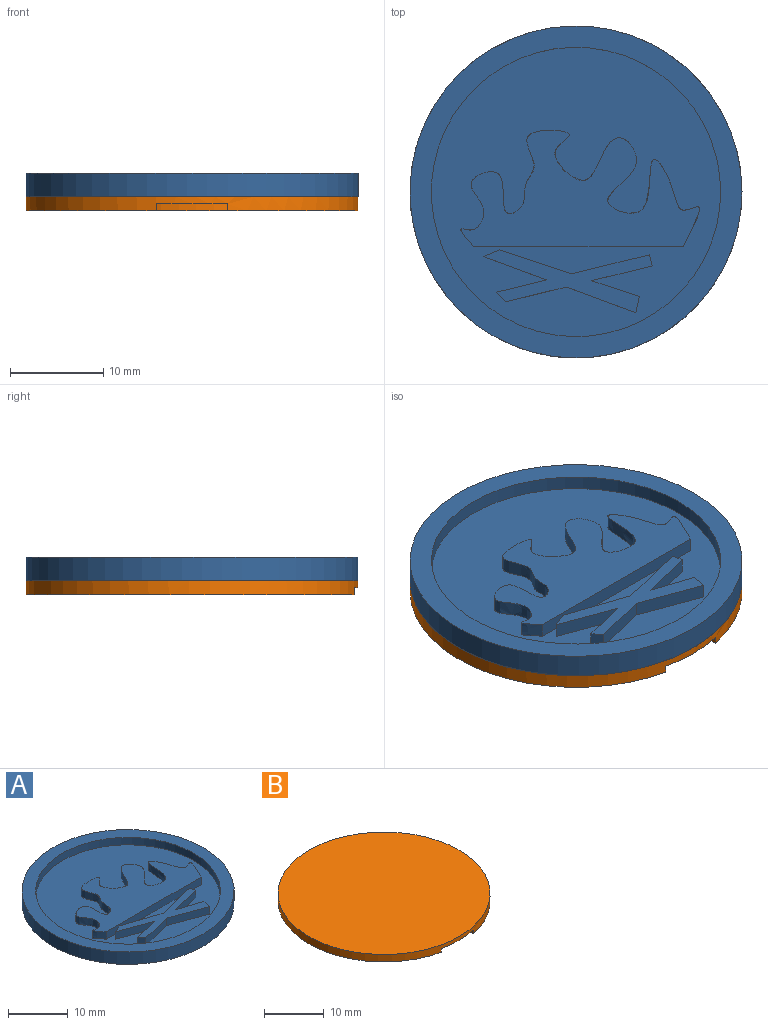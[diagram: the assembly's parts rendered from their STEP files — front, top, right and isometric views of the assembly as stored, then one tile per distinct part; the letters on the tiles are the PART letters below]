
ASSEMBLY  parts=2 mates=1
PART A: 21 faces, bbox 35.6x35.6x2.5 mm
  f0: plane 30.99x30.99mm, normal (0,0,1), area 534.1mm2, adj f4,f5,f6,f8,f9,f10,f11,f12
  f1: cylinder r=17.78mm len=35.56mm, axis (0,0,-1), area 283.8mm2, adj f2,f3
  f2: plane 35.56x35.56mm, normal (0,0,1), area 239mm2, adj f1,f4
  f3: plane 35.56x35.56mm, normal (0,0,-1), area 993.1mm2, adj f1
  f4: cylinder r=15.49mm len=30.99mm, axis (0,0,1), area 148.4mm2, adj f0,f2
  f5: extruded ~25.4x12.45mm, area 109.6mm2, adj f0,f6,f7
  f6: plane 22.45x1.52mm, normal (0,-1,0), area 34.2mm2, adj f0,f5,f7
  f7: plane 26.1x12.73mm, normal (0,0,1), area 178.2mm2, adj f5,f6
  f8: plane 7.73x2.57mm, normal (0.32,0.95,0), area 12.4mm2, adj f0,f9,f19,f20
  f9: plane 1.72x1.52mm, normal (-0.38,0.92,0), area 2.8mm2, adj f0,f8,f10,f20
  f10: plane 6.81x2.5mm, normal (-0.35,-0.94,0), area 11.1mm2, adj f0,f9,f11,f20
  f11: plane 5.37x1.52mm, normal (-0.24,0.97,0), area 8.4mm2, adj f0,f10,f12,f20
  f12: plane 1.52x1.04mm, normal (-0.76,-0.66,0), area 2.1mm2, adj f0,f11,f13,f20
  f13: plane 6.53x1.6mm, normal (0.24,-0.97,0), area 10.2mm2, adj f0,f12,f14,f20
  f14: plane 7.48x2.75mm, normal (-0.35,-0.94,0), area 12.1mm2, adj f0,f13,f15,f20
  f15: plane 1.74x1.52mm, normal (0.98,-0.21,0), area 2.7mm2, adj f0,f14,f16,f20
  f16: plane 5.08x1.69mm, normal (0.32,0.95,0), area 8.2mm2, adj f0,f15,f17,f20
  f17: plane 6.44x1.58mm, normal (0.24,-0.97,0), area 10.1mm2, adj f0,f16,f18,f20
  f18: plane 1.52x1.19mm, normal (0.97,0.24,0), area 1.9mm2, adj f0,f17,f19,f20
  f19: plane 8.34x2.05mm, normal (-0.24,0.97,0), area 13.1mm2, adj f0,f8,f18,f20
  f20: plane 18.08x6.73mm, normal (0,0,1), area 41.9mm2, adj f8,f9,f10,f11,f12,f13,f14,f15
PART B: 170 faces, bbox 35.6x35.6x1.5 mm
  f0: plane 30.99x30.99mm, normal (0,0,-1), area 549.6mm2, adj f4,f5,f6,f7,f8,f9,f10,f11
  f1: plane 35.56x35.15mm, normal (0,0,-1), area 175mm2, adj f2,f165,f167,f169
  f2: cylinder r=17.78mm len=35.56mm, axis (0,0,-1), area 164.4mm2, adj f1,f3,f165,f167,f168
  f3: plane 35.56x35.56mm, normal (0,0,1), area 993.1mm2, adj f2
  f4: plane 1.49x0.76mm, normal (0,-1,0), area 1.1mm2, adj f0,f5,f15,f16
  f5: plane 7.05x0.76mm, normal (-1,0,0), area 5.4mm2, adj f0,f4,f6,f16
  f6: plane 1.49x0.76mm, normal (0,1,0), area 1.1mm2, adj f0,f5,f7,f16
  f7: plane 2.76x0.76mm, normal (1,0,0), area 2.1mm2, adj f0,f6,f8,f16
  f8: plane 2.79x0.76mm, normal (0,1,0), area 2.1mm2, adj f0,f7,f9,f16
  f9: plane 2.76x0.76mm, normal (-1,0,0), area 2.1mm2, adj f0,f8,f10,f16
  f10: plane 1.5x0.76mm, normal (0,1,0), area 1.1mm2, adj f0,f9,f11,f16
  f11: plane 7.05x0.76mm, normal (1,0,0), area 5.4mm2, adj f0,f10,f12,f16
  f12: plane 1.5x0.76mm, normal (0,-1,0), area 1.1mm2, adj f0,f11,f13,f16
  f13: plane 3.04x0.76mm, normal (-1,0,0), area 2.3mm2, adj f0,f12,f14,f16
  f14: plane 2.79x0.76mm, normal (0,-1,0), area 2.1mm2, adj f0,f13,f15,f16
  f15: plane 3.04x0.76mm, normal (1,0,0), area 2.3mm2, adj f0,f4,f14,f16
  f16: plane 7.05x5.78mm, normal (0,0,-1), area 24.5mm2, adj f4,f5,f6,f7,f8,f9,f10,f11
  f17: plane 7.05x0.76mm, normal (-1,0,0), area 5.4mm2, adj f0,f18,f41,f42
  f18: plane 2.19x0.76mm, normal (0,1,0), area 1.7mm2, adj f0,f17,f19,f42
  f19: extruded ~2.18x0.76mm, area 1.7mm2, adj f0,f18,f20,f42
  f20: extruded ~1.36x0.76mm, area 1.2mm2, adj f0,f19,f21,f42
  f21: extruded ~1.04x0.76mm, area 0.8mm2, adj f0,f20,f22,f42
  f22: extruded ~0.79x0.76mm, area 0.7mm2, adj f0,f21,f23,f42
  f23: plane 0.76x0.05mm, normal (1,0,0), area 0mm2, adj f0,f22,f24,f42
  f24: extruded ~0.97x0.76mm, area 0.9mm2, adj f0,f23,f25,f42
  f25: extruded ~1.09x0.76mm, area 0.9mm2, adj f0,f24,f26,f42
  f26: extruded ~1.51x0.76mm, area 1.3mm2, adj f0,f25,f27,f42
  f27: extruded ~1.89x0.76mm, area 1.5mm2, adj f0,f26,f41,f42
  f28: plane 0.93x0.76mm, normal (0,-1,0), area 0.7mm2, adj f29,f39,f42,f44
  f29: plane 1.84x0.76mm, normal (1,0,0), area 1.4mm2, adj f28,f30,f42,f44
  f30: plane 0.97x0.76mm, normal (0,1,0), area 0.7mm2, adj f29,f31,f42,f44
  f31: extruded ~0.91x0.76mm, area 0.7mm2, adj f30,f32,f42,f44
  f32: extruded ~0.76x0.72mm, area 0.6mm2, adj f31,f39,f42,f44
  f33: plane 1.57x0.76mm, normal (1,0,0), area 1.2mm2, adj f34,f40,f42,f43
  f34: plane 0.87x0.76mm, normal (0,1,0), area 0.7mm2, adj f33,f35,f42,f43
  f35: extruded ~0.88x0.76mm, area 0.7mm2, adj f34,f36,f42,f43
  f36: extruded ~0.76x0.62mm, area 0.5mm2, adj f35,f37,f42,f43
  f37: extruded ~0.76x0.58mm, area 0.5mm2, adj f36,f38,f42,f43
  f38: extruded ~0.94x0.76mm, area 0.7mm2, adj f37,f40,f42,f43
  f39: extruded ~1.25x0.88mm, area 1.3mm2, adj f28,f32,f42,f44
  f40: plane 0.79x0.76mm, normal (0,-1,0), area 0.6mm2, adj f33,f38,f42,f43
  f41: plane 2.64x0.76mm, normal (0,-1,0), area 2mm2, adj f0,f17,f27,f42
  f42: plane 7.05x5.23mm, normal (0,0,-1), area 27.1mm2, adj f17,f18,f19,f20,f21,f22,f23,f24
  f43: plane 2.02x1.57mm, normal (0,0,-1), area 2.9mm2, adj f33,f34,f35,f36,f37,f38,f40
  f44: plane 2.18x1.84mm, normal (0,0,-1), area 3.6mm2, adj f28,f29,f30,f31,f32,f39
  f45: extruded ~2.44x2.09mm, area 2.8mm2, adj f0,f46,f52,f53
  f46: extruded ~2.44x2.09mm, area 2.8mm2, adj f0,f45,f47,f53
  f47: extruded ~2.41x2.09mm, area 2.7mm2, adj f0,f46,f52,f53
  f48: extruded ~1.63x1.14mm, area 1.7mm2, adj f49,f51,f53,f54
  f49: extruded ~1.63x1.14mm, area 1.7mm2, adj f48,f50,f53,f54
  f50: extruded ~1.6x1.14mm, area 1.7mm2, adj f49,f51,f53,f54
  f51: extruded ~1.6x1.14mm, area 1.7mm2, adj f48,f50,f53,f54
  f52: extruded ~2.41x2.09mm, area 2.7mm2, adj f0,f45,f47,f53
  f53: plane 4.85x4.18mm, normal (0,0,-1), area 10.4mm2, adj f45,f46,f47,f48,f49,f50,f51,f52
  f54: plane 3.24x2.27mm, normal (0,0,-1), area 6mm2, adj f48,f49,f50,f51
  f55: extruded ~1.45x0.82mm, area 1.3mm2, adj f0,f56,f62,f63
  f56: extruded ~1.6x1.45mm, area 1.9mm2, adj f0,f55,f57,f63
  f57: plane 3.16x0.76mm, normal (-1,0,0), area 2.4mm2, adj f0,f56,f58,f63
  f58: plane 0.93x0.76mm, normal (0,1,0), area 0.7mm2, adj f0,f57,f59,f63
  f59: plane 3.09x0.76mm, normal (1,0,0), area 2.4mm2, adj f0,f58,f60,f63
  f60: extruded ~0.86x0.76mm, area 0.9mm2, adj f0,f59,f61,f63
  f61: extruded ~0.76x0.69mm, area 0.7mm2, adj f0,f60,f62,f63
  f62: plane 0.76x0.64mm, normal (0.59,0.81,0), area 0.6mm2, adj f0,f55,f61,f63
  f63: plane 4.76x2.9mm, normal (0,0,-1), area 5.6mm2, adj f55,f56,f57,f58,f59,f60,f61,f62
  f64: extruded ~2.19x1.82mm, area 2.5mm2, adj f0,f65,f73,f74
  f65: extruded ~2.19x1.81mm, area 2.5mm2, adj f0,f64,f66,f74
  f66: plane 2.57x0.76mm, normal (-1,0,0), area 2mm2, adj f0,f65,f67,f74
  f67: plane 0.9x0.76mm, normal (0,1,0), area 0.7mm2, adj f0,f66,f68,f74
  f68: plane 2.65x0.76mm, normal (1,0,0), area 2mm2, adj f0,f67,f69,f74
  f69: extruded ~1.3x0.91mm, area 1.4mm2, adj f0,f68,f70,f74
  f70: extruded ~1.3x0.88mm, area 1.4mm2, adj f0,f69,f71,f74
  f71: plane 2.65x0.76mm, normal (-1,0,0), area 2mm2, adj f0,f70,f72,f74
  f72: plane 0.93x0.76mm, normal (0,1,0), area 0.7mm2, adj f0,f71,f73,f74
  f73: plane 2.57x0.76mm, normal (1,0,0), area 2mm2, adj f0,f64,f72,f74
  f74: plane 4.76x3.62mm, normal (0,0,-1), area 9.2mm2, adj f64,f65,f66,f67,f68,f69,f70,f71
  f75: plane 4.67x0.76mm, normal (1,0,0), area 3.6mm2, adj f0,f76,f90,f91
  f76: plane 0.88x0.76mm, normal (0,-1,0), area 0.7mm2, adj f0,f75,f77,f91
  f77: plane 1.88x0.76mm, normal (-1,0,0), area 1.4mm2, adj f0,f76,f78,f91
  f78: extruded ~1.63x0.76mm, area 1.2mm2, adj f0,f77,f79,f91
  f79: plane 0.76x0.03mm, normal (0,-1,0), area 0mm2, adj f0,f78,f80,f91
  f80: plane 1x0.76mm, normal (0.9,-0.43,0), area 0.8mm2, adj f0,f79,f81,f91
  f81: plane 2.5x1.35mm, normal (0.88,-0.48,0), area 2.2mm2, adj f0,f80,f82,f91
  f82: plane 0.95x0.76mm, normal (0,-1,0), area 0.7mm2, adj f0,f81,f83,f91
  f83: plane 4.67x0.76mm, normal (-1,0,0), area 3.6mm2, adj f0,f82,f84,f91
  f84: plane 0.88x0.76mm, normal (0,1,0), area 0.7mm2, adj f0,f83,f85,f91
  f85: plane 1.86x0.76mm, normal (1,0,0), area 1.4mm2, adj f0,f84,f86,f91
  f86: extruded ~1.64x0.76mm, area 1.3mm2, adj f0,f85,f87,f91
  f87: plane 0.76x0.03mm, normal (0,1,0), area 0mm2, adj f0,f86,f88,f91
  f88: plane 1.01x0.76mm, normal (-0.91,0.42,0), area 0.8mm2, adj f0,f87,f89,f91
  f89: plane 2.49x1.36mm, normal (-0.88,0.48,0), area 2.2mm2, adj f0,f88,f90,f91
  f90: plane 0.95x0.76mm, normal (0,1,0), area 0.7mm2, adj f0,f75,f89,f91
  f91: plane 4.67x3.57mm, normal (0,0,-1), area 10.9mm2, adj f75,f76,f77,f78,f79,f80,f81,f82
  f92: plane 2.41x1.31mm, normal (0.88,0.48,0), area 2.1mm2, adj f0,f93,f109,f110
  f93: plane 0.99x0.76mm, normal (0,-1,0), area 0.8mm2, adj f0,f92,f94,f110
  f94: plane 1.04x0.76mm, normal (-0.9,-0.43,0), area 0.9mm2, adj f0,f93,f95,f110
  f95: extruded ~0.77x0.76mm, area 0.6mm2, adj f0,f94,f96,f110
  f96: plane 0.76x0.02mm, normal (0,-1,0), area 0mm2, adj f0,f95,f97,f110
  f97: extruded ~0.77x0.76mm, area 0.6mm2, adj f0,f96,f98,f110
  f98: plane 1.04x0.76mm, normal (0.89,-0.45,0), area 0.9mm2, adj f0,f97,f99,f110
  f99: plane 1.04x0.76mm, normal (0,-1,0), area 0.8mm2, adj f0,f98,f100,f110
  f100: plane 2.37x1.31mm, normal (-0.87,0.48,0), area 2.1mm2, adj f0,f99,f101,f110
  f101: plane 2.3x1.23mm, normal (-0.88,-0.47,0), area 2mm2, adj f0,f100,f102,f110
  f102: plane 0.98x0.76mm, normal (0,1,0), area 0.8mm2, adj f0,f101,f103,f110
  f103: plane 0.96x0.76mm, normal (0.91,0.42,0), area 0.8mm2, adj f0,f102,f104,f110
  f104: extruded ~0.76x0.74mm, area 0.6mm2, adj f0,f103,f105,f110
  f105: plane 0.76x0.03mm, normal (0,1,0), area 0mm2, adj f0,f104,f106,f110
  f106: extruded ~0.76x0.74mm, area 0.6mm2, adj f0,f105,f107,f110
  f107: plane 0.96x0.76mm, normal (-0.9,0.44,0), area 0.8mm2, adj f0,f106,f108,f110
  f108: plane 1.04x0.76mm, normal (0,1,0), area 0.8mm2, adj f0,f107,f109,f110
  f109: plane 2.26x1.23mm, normal (0.88,-0.48,0), area 2mm2, adj f0,f92,f108,f110
  f110: plane 4.67x3.78mm, normal (0,0,-1), area 8.4mm2, adj f92,f93,f94,f95,f96,f97,f98,f99
  f111: plane 4.67x0.76mm, normal (1,0,0), area 3.6mm2, adj f0,f112,f114,f115
  f112: plane 0.94x0.76mm, normal (0,-1,0), area 0.7mm2, adj f0,f111,f113,f115
  f113: plane 4.67x0.76mm, normal (-1,0,0), area 3.6mm2, adj f0,f112,f114,f115
  f114: plane 0.94x0.76mm, normal (0,1,0), area 0.7mm2, adj f0,f111,f113,f115
  f115: plane 4.67x0.94mm, normal (0,0,-1), area 4.4mm2, adj f111,f112,f113,f114
  f116: plane 4.67x0.76mm, normal (1,0,0), area 3.6mm2, adj f0,f117,f131,f132
  f117: plane 0.88x0.76mm, normal (0,-1,0), area 0.7mm2, adj f0,f116,f118,f132
  f118: plane 1.88x0.76mm, normal (-1,0,0), area 1.4mm2, adj f0,f117,f119,f132
  f119: extruded ~1.63x0.76mm, area 1.2mm2, adj f0,f118,f120,f132
  f120: plane 0.76x0.03mm, normal (0,-1,0), area 0mm2, adj f0,f119,f121,f132
  f121: plane 1x0.76mm, normal (0.9,-0.43,0), area 0.8mm2, adj f0,f120,f122,f132
  f122: plane 2.5x1.35mm, normal (0.88,-0.48,0), area 2.2mm2, adj f0,f121,f123,f132
  f123: plane 0.95x0.76mm, normal (0,-1,0), area 0.7mm2, adj f0,f122,f124,f132
  f124: plane 4.67x0.76mm, normal (-1,0,0), area 3.6mm2, adj f0,f123,f125,f132
  f125: plane 0.88x0.76mm, normal (0,1,0), area 0.7mm2, adj f0,f124,f126,f132
  f126: plane 1.86x0.76mm, normal (1,0,0), area 1.4mm2, adj f0,f125,f127,f132
  f127: extruded ~1.64x0.76mm, area 1.3mm2, adj f0,f126,f128,f132
  f128: plane 0.76x0.03mm, normal (0,1,0), area 0mm2, adj f0,f127,f129,f132
  f129: plane 1.01x0.76mm, normal (-0.91,0.42,0), area 0.8mm2, adj f0,f128,f130,f132
  f130: plane 2.49x1.36mm, normal (-0.88,0.48,0), area 2.2mm2, adj f0,f129,f131,f132
  f131: plane 0.95x0.76mm, normal (0,1,0), area 0.7mm2, adj f0,f116,f130,f132
  f132: plane 4.67x3.57mm, normal (0,0,-1), area 10.9mm2, adj f116,f117,f118,f119,f120,f121,f122,f123
  f133: extruded ~1.78x0.76mm, area 1.4mm2, adj f134,f146,f147,f163
  f134: extruded ~1.78x0.76mm, area 1.4mm2, adj f133,f135,f147,f163
  f135: extruded ~1.35x0.76mm, area 1.2mm2, adj f134,f136,f147,f163
  f136: extruded ~2.38x1.78mm, area 2.6mm2, adj f135,f137,f147,f163
  f137: extruded ~2.38x1.79mm, area 2.6mm2, adj f136,f146,f147,f163
  f138: extruded ~2.69x0.87mm, area 2.2mm2, adj f0,f139,f145,f147
  f139: extruded ~2.69x0.86mm, area 2.2mm2, adj f0,f138,f140,f147
  f140: extruded ~2.49x0.94mm, area 2.1mm2, adj f0,f139,f141,f147
  f141: extruded ~2.5x0.93mm, area 2.1mm2, adj f0,f140,f142,f147
  f142: extruded ~2.69x0.87mm, area 2.2mm2, adj f0,f141,f143,f147
  f143: extruded ~2.7x0.87mm, area 2.2mm2, adj f0,f142,f144,f147
  f144: extruded ~2.49x0.94mm, area 2.1mm2, adj f0,f143,f145,f147
  f145: extruded ~2.49x0.94mm, area 2.1mm2, adj f0,f138,f144,f147
  f146: extruded ~1.34x0.76mm, area 1.2mm2, adj f133,f137,f147,f163
  f147: plane 7.26x6.71mm, normal (0,0,-1), area 26mm2, adj f133,f134,f135,f136,f137,f138,f139,f140
  f148: extruded ~1.78x0.76mm, area 1.4mm2, adj f149,f161,f162,f164
  f149: extruded ~1.78x0.76mm, area 1.4mm2, adj f148,f150,f162,f164
  f150: extruded ~1.35x0.76mm, area 1.2mm2, adj f149,f151,f162,f164
  f151: extruded ~2.38x1.78mm, area 2.6mm2, adj f150,f152,f162,f164
  f152: extruded ~2.38x1.79mm, area 2.6mm2, adj f151,f161,f162,f164
  f153: extruded ~2.69x0.87mm, area 2.2mm2, adj f0,f154,f160,f162
  f154: extruded ~2.69x0.86mm, area 2.2mm2, adj f0,f153,f155,f162
  f155: extruded ~2.49x0.94mm, area 2.1mm2, adj f0,f154,f156,f162
  f156: extruded ~2.5x0.93mm, area 2.1mm2, adj f0,f155,f157,f162
  f157: extruded ~2.69x0.87mm, area 2.2mm2, adj f0,f156,f158,f162
  f158: extruded ~2.7x0.87mm, area 2.2mm2, adj f0,f157,f159,f162
  f159: extruded ~2.49x0.94mm, area 2.1mm2, adj f0,f158,f160,f162
  f160: extruded ~2.49x0.94mm, area 2.1mm2, adj f0,f153,f159,f162
  f161: extruded ~1.34x0.76mm, area 1.2mm2, adj f148,f152,f162,f164
  f162: plane 7.26x6.71mm, normal (0,0,-1), area 26mm2, adj f148,f149,f150,f151,f152,f153,f154,f155
  f163: plane 4.76x3.58mm, normal (0,0,-1), area 14.2mm2, adj f133,f134,f135,f136,f137,f146
  f164: plane 4.76x3.58mm, normal (0,0,-1), area 14.2mm2, adj f148,f149,f150,f151,f152,f161
  f165: plane 1.83x0.76mm, normal (1,0,0), area 1.4mm2, adj f1,f2,f168,f169
  f166: cylinder r=15.49mm len=30.99mm, axis (0,0,-1), area 74.2mm2, adj f0,f168
  f167: plane 1.83x0.76mm, normal (-1,0,0), area 1.4mm2, adj f1,f2,f168,f169
  f168: plane 33.78x32mm, normal (0,0,-1), area 63.9mm2, adj f2,f165,f166,f167,f169
  f169: cylinder r=16mm len=32mm, axis (0,0,-1), area 70.8mm2, adj f1,f165,f167,f168
PLACE A t=(-6.45,-25.08,-32.14)mm fixed
PLACE B t=(-6.45,-25.08,-33.67)mm
MATE fastened A.f1 <-> B.f2  axis (0,0,-1) through (-6.45,-25.08,-32.14)mm
